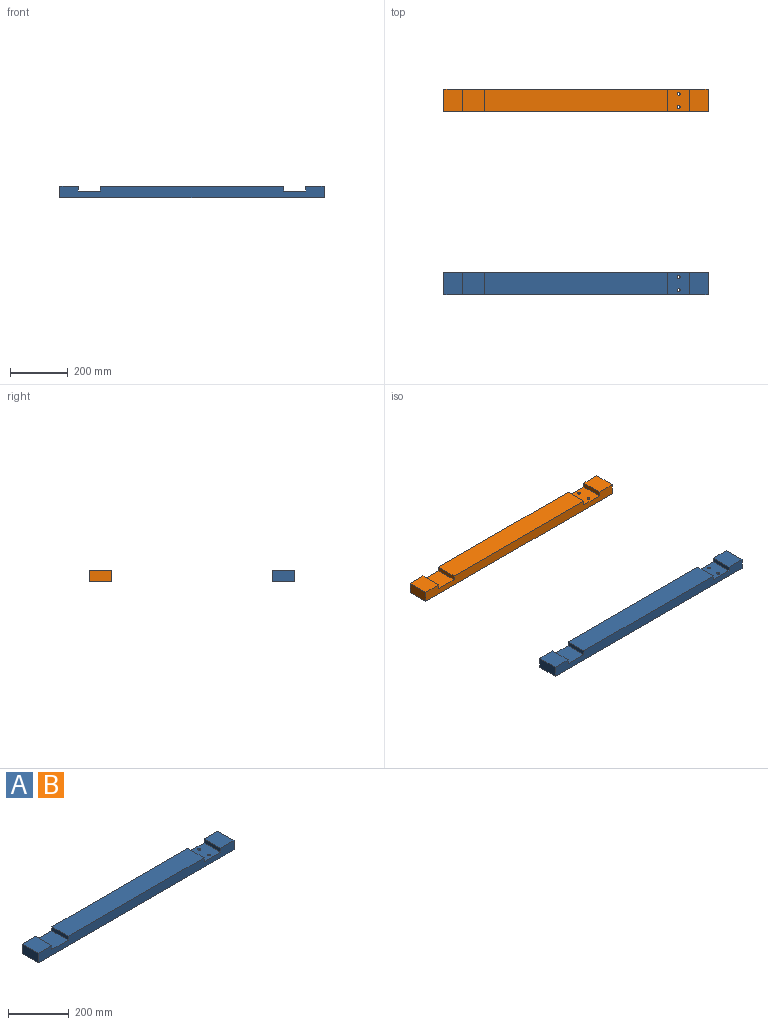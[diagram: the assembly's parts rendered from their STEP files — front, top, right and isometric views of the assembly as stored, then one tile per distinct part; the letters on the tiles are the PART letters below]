
ASSEMBLY  parts=2 mates=2
PART A: 16 faces, bbox 914.4x76.2x38.1 mm
  f0: plane 914.4x76.2mm, normal (0,0,-1), area 69522.7mm2, adj f1,f7,f8,f9,f14,f15
  f1: plane 76.2x38.1mm, normal (1,0,0), area 2903.2mm2, adj f0,f2,f7,f8
  f2: plane 76.2x63.5mm, normal (0,0,1), area 4838.7mm2, adj f1,f3,f7,f8
  f3: plane 76.2x15.88mm, normal (-1,0,0), area 1209.7mm2, adj f2,f4,f7,f8
  f4: plane 76.2x76.2mm, normal (0,0,1), area 5651.8mm2, adj f3,f5,f7,f8,f14,f15
  f5: plane 76.2x15.88mm, normal (1,0,0), area 1209.7mm2, adj f4,f6,f7,f8
  f6: plane 635x76.2mm, normal (0,0,1), area 48387mm2, adj f5,f7,f8,f13
  f7: plane 914.4x38.1mm, normal (0,-1,0), area 32419.3mm2, adj f0,f1,f2,f3,f4,f5,f6,f9
  f8: plane 914.4x38.1mm, normal (0,1,0), area 32419.3mm2, adj f0,f1,f2,f3,f4,f5,f6,f9
  f9: plane 76.2x38.1mm, normal (-1,0,0), area 2903.2mm2, adj f0,f7,f8,f10
  f10: plane 76.2x63.5mm, normal (0,0,1), area 4838.7mm2, adj f7,f8,f9,f11
  f11: plane 76.2x15.88mm, normal (1,0,0), area 1209.7mm2, adj f7,f8,f10,f12
  f12: plane 76.2x76.2mm, normal (0,0,1), area 5806.4mm2, adj f7,f8,f11,f13
  f13: plane 76.2x15.88mm, normal (-1,0,0), area 1209.7mm2, adj f6,f7,f8,f12
  f14: cylinder r=4.96mm len=22.23mm, axis (0,0,1), area 692.7mm2, adj f0,f4
  f15: cylinder r=4.96mm len=22.23mm, axis (0,0,1), area 692.7mm2, adj f0,f4
PART B: same geometry as A
PLACE A t=(-83.31,424.16,-30.62)mm
PLACE B t=(-83.31,1059.16,-30.62)mm
MATE parallel A.f7 <-> B.f8  axis (0,-1,0) through (-83.31,347.96,-12.4)mm
MATE parallel B.f1 <-> A.f1  axis (1,0,0) through (373.89,1021.06,-11.57)mm
